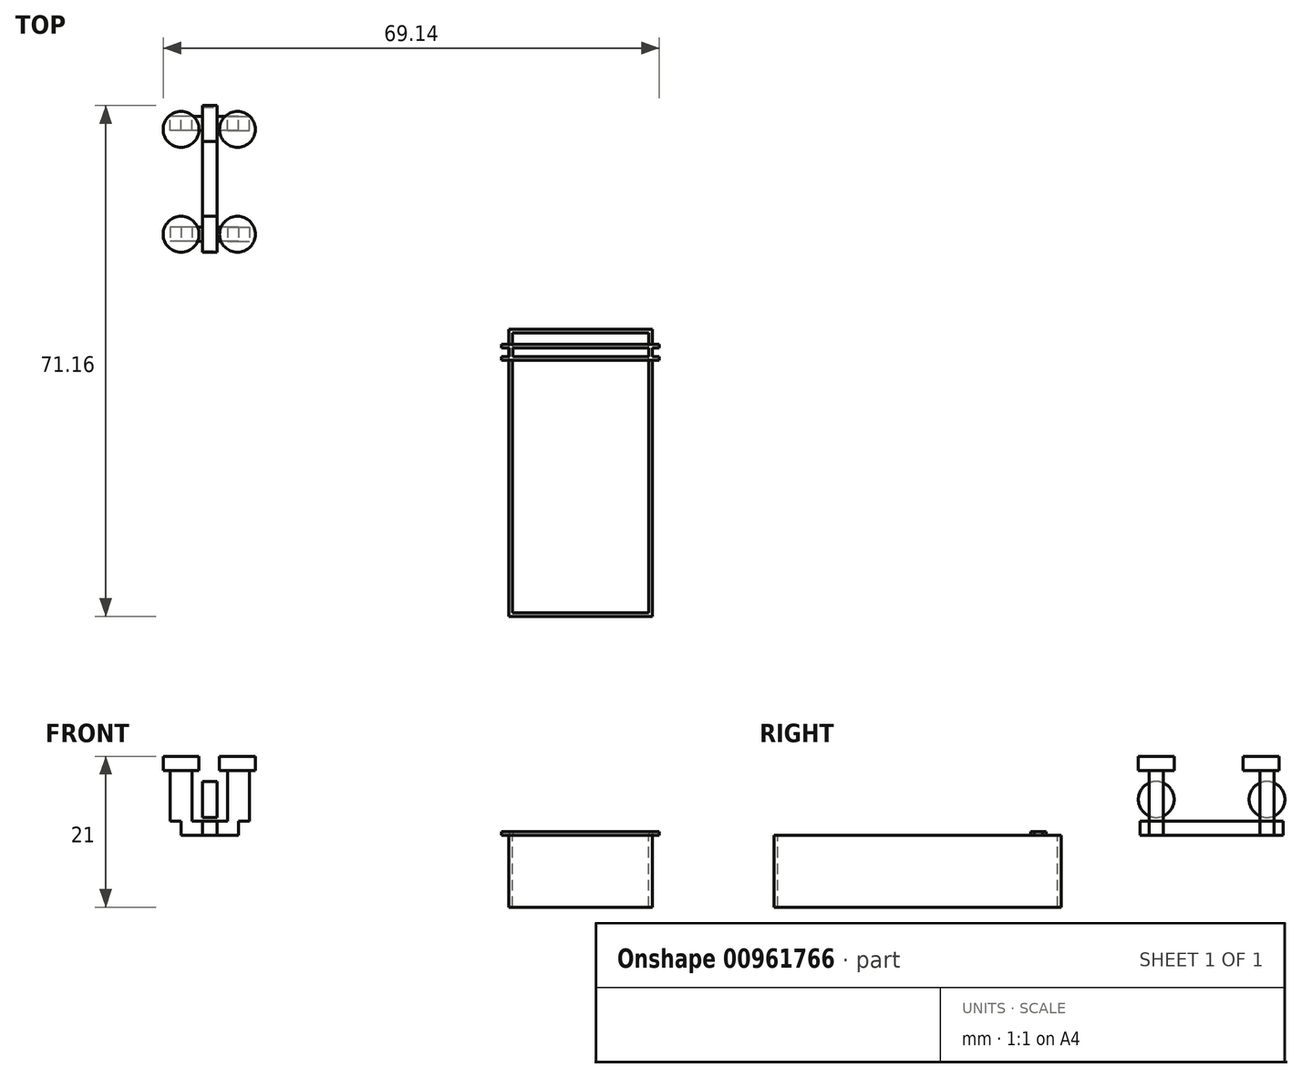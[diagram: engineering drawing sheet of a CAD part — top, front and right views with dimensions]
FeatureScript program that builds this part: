
annotation { "Feature Type Name" : "Feature", "Feature Type Description" : "" }
export const myFeature = defineFeature(function(context is Context, id is Id, definition is map)
    precondition{}
    {
        {
            var Q0;
            Q0=qCreatedBy(makeId("Top.planeOp"),FACE);
            var sketch = newSketch(context, id + "F0", { "sketchPlane" : qUnion([Q0])});
            skLineSegment(sketch, "E0.bottom", {"start": v(-9.2, 17.34) * mm, "end": v(10.8, 17.34) * mm});
            skLineSegment(sketch, "E0.top", {"start": v(-9.2, -22.66) * mm, "end": v(10.8, -22.66) * mm});
            skLineSegment(sketch, "E0.left", {"start": v(-9.2, 17.34) * mm, "end": v(-9.2, -22.66) * mm});
            skLineSegment(sketch, "E0.right", {"start": v(10.8, 17.34) * mm, "end": v(10.8, -22.66) * mm});
            skLineSegment(sketch, "E1.0", {"start": v(-8.7, 16.84) * mm, "end": v(10.3, 16.84) * mm});
            skLineSegment(sketch, "E1.1", {"start": v(-8.7, 16.84) * mm, "end": v(-8.7, -22.16) * mm});
            skLineSegment(sketch, "E1.2", {"start": v(-8.7, -22.16) * mm, "end": v(10.3, -22.16) * mm});
            skLineSegment(sketch, "E1.3", {"start": v(10.3, 16.84) * mm, "end": v(10.3, -22.16) * mm});
            skSolve(sketch);
        }
        {
            var Q0;
            Q0 = qSketchRegion(id + "F0", true);
            extrude(context, id + "F1", {"entities" : qUnion([Q0]), "depth" : -10 * mm, "offsetDistance" : 25 * mm});
        }
        {
            var Q0;
            Q0=qCreatedBy(makeId("Top.planeOp"),FACE);
            var sketch = newSketch(context, id + "F2", { "sketchPlane" : qUnion([Q0])});
            skLineSegment(sketch, "E2.bottom", {"start": v(-10.2, 15.22) * mm, "end": v(11.8, 15.22) * mm});
            skLineSegment(sketch, "E2.top", {"start": v(-10.2, 14.72) * mm, "end": v(11.8, 14.72) * mm});
            skLineSegment(sketch, "E2.left", {"start": v(-10.2, 15.22) * mm, "end": v(-10.2, 14.72) * mm});
            skLineSegment(sketch, "E2.right", {"start": v(11.8, 15.22) * mm, "end": v(11.8, 14.72) * mm});
            skLineSegment(sketch, "E3.bottom", {"start": v(-10.2, 13.55) * mm, "end": v(11.8, 13.55) * mm});
            skLineSegment(sketch, "E3.top", {"start": v(-10.2, 13.05) * mm, "end": v(11.8, 13.05) * mm});
            skLineSegment(sketch, "E3.left", {"start": v(-10.2, 13.55) * mm, "end": v(-10.2, 13.05) * mm});
            skLineSegment(sketch, "E3.right", {"start": v(11.8, 13.55) * mm, "end": v(11.8, 13.05) * mm});
            skLineSegment(sketch, "E4.bottom", {"start": v(-9.15, 15.22) * mm, "end": v(-8.62, 15.22) * mm});
            skLineSegment(sketch, "E4.top", {"start": v(-9.15, 13.05) * mm, "end": v(-8.62, 13.05) * mm});
            skLineSegment(sketch, "E4.left", {"start": v(-9.15, 15.22) * mm, "end": v(-9.15, 13.05) * mm});
            skLineSegment(sketch, "E4.right", {"start": v(-8.62, 15.22) * mm, "end": v(-8.62, 13.05) * mm});
            skLineSegment(sketch, "E5.bottom", {"start": v(10.81, 15.22) * mm, "end": v(10.29, 15.22) * mm});
            skLineSegment(sketch, "E5.top", {"start": v(10.81, 13.05) * mm, "end": v(10.29, 13.05) * mm});
            skLineSegment(sketch, "E5.left", {"start": v(10.81, 15.22) * mm, "end": v(10.81, 13.05) * mm});
            skLineSegment(sketch, "E5.right", {"start": v(10.29, 15.22) * mm, "end": v(10.29, 13.05) * mm});
            skSolve(sketch);
        }
        {
            var Q0;
            Q0 = qSketchRegion(id + "F2", true);
            extrude(context, id + "F3", {"entities" : qUnion([Q0]), "operationType" : NewBodyOperationType.ADD, "depth" : 0.5 * mm, "offsetDistance" : 25 * mm});
        }
        {
            var Q0;
            Q0=qCreatedBy(makeId("Top.planeOp"),FACE);
            var sketch = newSketch(context, id + "F4", { "sketchPlane" : qUnion([Q0])});
            skLineSegment(sketch, "E6.bottom", {"start": v(-51.85, 48.28) * mm, "end": v(-49.85, 48.28) * mm});
            skLineSegment(sketch, "E6.top", {"start": v(-51.85, 28.28) * mm, "end": v(-49.85, 28.28) * mm});
            skLineSegment(sketch, "E6.left", {"start": v(-51.85, 48.28) * mm, "end": v(-51.85, 28.28) * mm});
            skLineSegment(sketch, "E6.right", {"start": v(-49.85, 48.28) * mm, "end": v(-49.85, 28.28) * mm});
            skLineSegment(sketch, "E7.bottom", {"start": v(-46.85, 45) * mm, "end": v(-54.85, 45) * mm});
            skLineSegment(sketch, "E7.top", {"start": v(-46.85, 47) * mm, "end": v(-54.85, 47) * mm});
            skLineSegment(sketch, "E7.left", {"start": v(-46.85, 45) * mm, "end": v(-46.85, 47) * mm});
            skLineSegment(sketch, "E7.right", {"start": v(-54.85, 45) * mm, "end": v(-54.85, 47) * mm});
            skLineSegment(sketch, "E8.MirrorCS", {"start": v(-46.85, 31.56) * mm, "end": v(-54.85, 31.56) * mm});
            skLineSegment(sketch, "E9.MirrorCS", {"start": v(-54.85, 31.56) * mm, "end": v(-54.85, 29.56) * mm});
            skLineSegment(sketch, "E10.MirrorCS", {"start": v(-46.85, 29.56) * mm, "end": v(-54.85, 29.56) * mm});
            skLineSegment(sketch, "E11.MirrorCS", {"start": v(-46.85, 31.56) * mm, "end": v(-46.85, 29.56) * mm});
            skCircle(sketch, "E12", {"center": v(-46.86, 46.1) * mm, "radius": 2.5 * mm});
            skCircle(sketch, "E13", {"center": v(-54.85, 46) * mm, "radius": 2.5 * mm});
            skCircle(sketch, "E14.MirrorC", {"center": v(-46.86, 30.46) * mm, "radius": 2.5 * mm});
            skCircle(sketch, "E15.MirrorC", {"center": v(-54.85, 30.56) * mm, "radius": 2.5 * mm});
            skCircle(sketch, "E16", {"center": v(-54.85, 46) * mm, "radius": 0.7 * mm});
            skCircle(sketch, "E17.MirrorC", {"center": v(-54.85, 30.56) * mm, "radius": 0.7 * mm});
            skCircle(sketch, "E18.MirrorC", {"center": v(-46.85, 46) * mm, "radius": 0.7 * mm});
            skCircle(sketch, "E19.MirrorC", {"center": v(-46.85, 30.56) * mm, "radius": 0.7 * mm});
            skSolve(sketch);
        }
        {
            var Q0;
            {var subQ0=sQuery(id+"F4.wireOp",EDGE,"E6.bottom");Q0=makeQuery(id+"F4.imprint","IMPRINT",FACE,{"disambiguationData":[TD([[makeQuery(id+"F4.imprint","IMPRINT",EDGE,{"derivedFrom":subQ0}),-1.0]])]});}
            var Q1;
            {var subQ0=sQuery(id+"F4.wireOp",EDGE,"E6.top");Q1=makeQuery(id+"F4.imprint","IMPRINT",FACE,{"disambiguationData":[TD([[makeQuery(id+"F4.imprint","IMPRINT",EDGE,{"derivedFrom":subQ0}),1.0]])]});}
            var Q2;
            {var subQ0=sQuery(id+"F4.wireOp",EDGE,"E7.top");var subQ1=sQuery(id+"F4.wireOp",EDGE,"E6.left");var subQ2=makeQuery(id+"F4.imprint","INTERSECT",VERTEX,{"derivedFrom":[subQ1,subQ0]});Q2=makeQuery(id+"F4.imprint","IMPRINT",FACE,{"disambiguationData":[TD([[makeQuery(id+"F4.imprint","IMPRINT",EDGE,{"disambiguationData":[TD([[subQ2,-1.0]])],"derivedFrom":subQ1}),-1.0]])]});}
            var Q3;
            {var subQ0=sQuery(id+"F4.wireOp",EDGE,"E7.bottom");var subQ1=sQuery(id+"F4.wireOp",EDGE,"E6.left");var subQ2=makeQuery(id+"F4.imprint","INTERSECT",VERTEX,{"derivedFrom":[subQ1,subQ0]});Q3=makeQuery(id+"F4.imprint","IMPRINT",FACE,{"disambiguationData":[TD([[makeQuery(id+"F4.imprint","IMPRINT",EDGE,{"disambiguationData":[TD([[subQ2,-1.0]])],"derivedFrom":subQ1}),1.0]])]});}
            var Q4;
            {var subQ0=sQuery(id+"F4.wireOp",EDGE,"E8.MirrorCS");var subQ1=sQuery(id+"F4.wireOp",EDGE,"E6.left");var subQ2=makeQuery(id+"F4.imprint","INTERSECT",VERTEX,{"derivedFrom":[subQ1,subQ0]});Q4=makeQuery(id+"F4.imprint","IMPRINT",FACE,{"disambiguationData":[TD([[makeQuery(id+"F4.imprint","IMPRINT",EDGE,{"disambiguationData":[TD([[subQ2,-1.0]])],"derivedFrom":subQ1}),-1.0]])]});}
            var Q5;
            {var subQ0=sQuery(id+"F4.wireOp",EDGE,"E7.top");var subQ1=sQuery(id+"F4.wireOp",EDGE,"E6.right");var subQ2=makeQuery(id+"F4.imprint","INTERSECT",VERTEX,{"derivedFrom":[subQ1,subQ0]});Q5=makeQuery(id+"F4.imprint","IMPRINT",FACE,{"disambiguationData":[TD([[makeQuery(id+"F4.imprint","IMPRINT",EDGE,{"disambiguationData":[TD([[subQ2,-1.0]])],"derivedFrom":subQ1}),1.0]])]});}
            var Q6;
            {var subQ0=sQuery(id+"F4.wireOp",EDGE,"E8.MirrorCS");var subQ1=sQuery(id+"F4.wireOp",EDGE,"E6.right");var subQ2=makeQuery(id+"F4.imprint","INTERSECT",VERTEX,{"derivedFrom":[subQ1,subQ0]});Q6=makeQuery(id+"F4.imprint","IMPRINT",FACE,{"disambiguationData":[TD([[makeQuery(id+"F4.imprint","IMPRINT",EDGE,{"disambiguationData":[TD([[subQ2,-1.0]])],"derivedFrom":subQ1}),1.0]])]});}
            var Q7;
            {var subQ0=sQuery(id+"F4.wireOp",EDGE,"E7.left");var subQ6=sQuery(id+"F4.wireOp",EDGE,"E7.bottom");var subQ7=makeQuery(id+"F4.imprint","INTERSECT",VERTEX,{"derivedFrom":[subQ6,subQ0]});Q7=makeQuery(id+"F4.imprint","IMPRINT",FACE,{"disambiguationData":[TD([[makeQuery(id+"F4.imprint","IMPRINT",EDGE,{"disambiguationData":[TD([[subQ7,-1.0]])],"derivedFrom":subQ6}),-1.0]])]});}
            var Q8;
            {var subQ0=sQuery(id+"F4.wireOp",EDGE,"E11.MirrorCS");var subQ1=sQuery(id+"F4.wireOp",EDGE,"E8.MirrorCS");var subQ2=makeQuery(id+"F4.imprint","INTERSECT",VERTEX,{"derivedFrom":[subQ1,subQ0]});Q8=makeQuery(id+"F4.imprint","IMPRINT",FACE,{"disambiguationData":[TD([[makeQuery(id+"F4.imprint","IMPRINT",EDGE,{"disambiguationData":[TD([[subQ2,-1.0]])],"derivedFrom":subQ1}),1.0]])]});}
            var Q9;
            {var subQ1=sQuery(id+"F4.wireOp",EDGE,"E9.MirrorCS");var subQ5=sQuery(id+"F4.wireOp",EDGE,"E8.MirrorCS");var subQ9=makeQuery(id+"F4.imprint","INTERSECT",VERTEX,{"derivedFrom":[subQ5,subQ1]});Q9=makeQuery(id+"F4.imprint","IMPRINT",FACE,{"disambiguationData":[TD([[makeQuery(id+"F4.imprint","IMPRINT",EDGE,{"disambiguationData":[TD([[subQ9,1.0]])],"derivedFrom":subQ5}),1.0]])]});}
            var Q10;
            {var subQ0=sQuery(id+"F4.wireOp",EDGE,"E7.top");var subQ1=sQuery(id+"F4.wireOp",EDGE,"E6.left");var subQ2=makeQuery(id+"F4.imprint","INTERSECT",VERTEX,{"derivedFrom":[subQ1,subQ0]});Q10=makeQuery(id+"F4.imprint","IMPRINT",FACE,{"disambiguationData":[TD([[makeQuery(id+"F4.imprint","IMPRINT",EDGE,{"disambiguationData":[TD([[subQ2,-1.0]])],"derivedFrom":subQ1}),1.0]])]});}
            var Q11;
            {var subQ0=sQuery(id+"F4.wireOp",EDGE,"E8.MirrorCS");var subQ1=sQuery(id+"F4.wireOp",EDGE,"E6.left");var subQ2=makeQuery(id+"F4.imprint","INTERSECT",VERTEX,{"derivedFrom":[subQ1,subQ0]});Q11=makeQuery(id+"F4.imprint","IMPRINT",FACE,{"disambiguationData":[TD([[makeQuery(id+"F4.imprint","IMPRINT",EDGE,{"disambiguationData":[TD([[subQ2,-1.0]])],"derivedFrom":subQ1}),1.0]])]});}
            var Q12;
            {var subQ0=sQuery(id+"F4.wireOp",EDGE,"E7.right");var subQ5=sQuery(id+"F4.wireOp",EDGE,"E7.bottom");var subQ6=makeQuery(id+"F4.imprint","INTERSECT",VERTEX,{"derivedFrom":[subQ5,subQ0]});Q12=makeQuery(id+"F4.imprint","IMPRINT",FACE,{"disambiguationData":[TD([[makeQuery(id+"F4.imprint","IMPRINT",EDGE,{"disambiguationData":[TD([[subQ6,1.0]])],"derivedFrom":subQ5}),-1.0]])]});}
            var Q13;
            {var subQ0=sQuery(id+"F4.wireOp",EDGE,"E16");var subQ1=sQuery(id+"F4.wireOp",EDGE,"E7.right");var subQ2=makeQuery(id+"F4.imprint","INTERSECT",VERTEX,{"disambiguationData":[OD(0.0)],"derivedFrom":[subQ1,subQ0]});Q13=makeQuery(id+"F4.imprint","IMPRINT",FACE,{"disambiguationData":[TD([[makeQuery(id+"F4.imprint","IMPRINT",EDGE,{"disambiguationData":[TD([[subQ2,-1.0]])],"derivedFrom":subQ1}),-1.0]])]});}
            var Q14;
            {var subQ0=sQuery(id+"F4.wireOp",EDGE,"E18.MirrorC");var subQ1=sQuery(id+"F4.wireOp",EDGE,"E7.left");var subQ2=makeQuery(id+"F4.imprint","INTERSECT",VERTEX,{"disambiguationData":[OD(0.0)],"derivedFrom":[subQ1,subQ0]});Q14=makeQuery(id+"F4.imprint","IMPRINT",FACE,{"disambiguationData":[TD([[makeQuery(id+"F4.imprint","IMPRINT",EDGE,{"disambiguationData":[TD([[subQ2,-1.0]])],"derivedFrom":subQ1}),1.0]])]});}
            var Q15;
            {var subQ0=sQuery(id+"F4.wireOp",EDGE,"E19.MirrorC");var subQ1=sQuery(id+"F4.wireOp",EDGE,"E11.MirrorCS");var subQ2=makeQuery(id+"F4.imprint","INTERSECT",VERTEX,{"disambiguationData":[OD(0.0)],"derivedFrom":[subQ1,subQ0]});Q15=makeQuery(id+"F4.imprint","IMPRINT",FACE,{"disambiguationData":[TD([[makeQuery(id+"F4.imprint","IMPRINT",EDGE,{"disambiguationData":[TD([[subQ2,-1.0]])],"derivedFrom":subQ1}),-1.0]])]});}
            var Q16;
            {var subQ0=sQuery(id+"F4.wireOp",EDGE,"E17.MirrorC");var subQ1=sQuery(id+"F4.wireOp",EDGE,"E9.MirrorCS");var subQ2=makeQuery(id+"F4.imprint","INTERSECT",VERTEX,{"disambiguationData":[OD(0.0)],"derivedFrom":[subQ1,subQ0]});Q16=makeQuery(id+"F4.imprint","IMPRINT",FACE,{"disambiguationData":[TD([[makeQuery(id+"F4.imprint","IMPRINT",EDGE,{"disambiguationData":[TD([[subQ2,-1.0]])],"derivedFrom":subQ1}),1.0]])]});}
            extrude(context, id + "F5", {"entities" : qUnion([Q0, Q1, Q2, Q3, Q4, Q5, Q6, Q7, Q8, Q9, Q10, Q11, Q12, Q13, Q14, Q15, Q16]), "depth" : 2 * mm, "offsetDistance" : 25 * mm});
        }
        {
            var Q0;
            Q0=makeQuery(id+"F5.opExtrude","CAP_FACE",FACE,{"disambiguationData":[OSD([sQuery(id+"F4.wireOp",EDGE,"E6.bottom"),sQuery(id+"F4.wireOp",EDGE,"E6.top"),sQuery(id+"F4.wireOp",EDGE,"E6.left"),sQuery(id+"F4.wireOp",EDGE,"E6.right"),sQuery(id+"F4.wireOp",EDGE,"E7.bottom"),sQuery(id+"F4.wireOp",EDGE,"E7.top"),sQuery(id+"F4.wireOp",EDGE,"E7.left"),sQuery(id+"F4.wireOp",EDGE,"E7.right"),sQuery(id+"F4.wireOp",EDGE,"E8.MirrorCS"),sQuery(id+"F4.wireOp",EDGE,"E9.MirrorCS"),sQuery(id+"F4.wireOp",EDGE,"E10.MirrorCS"),sQuery(id+"F4.wireOp",EDGE,"E11.MirrorCS")])],"isStart":false});
            var sketch = newSketch(context, id + "F6", { "sketchPlane" : qUnion([Q0])});
            skLineSegment(sketch, "E20.bottom", {"start": v(-53.35, 45) * mm, "end": v(-56.35, 45) * mm});
            skLineSegment(sketch, "E20.top", {"start": v(-53.35, 47) * mm, "end": v(-56.35, 47) * mm});
            skLineSegment(sketch, "E20.left", {"start": v(-53.35, 45) * mm, "end": v(-53.35, 47) * mm});
            skLineSegment(sketch, "E20.right", {"start": v(-56.35, 45) * mm, "end": v(-56.35, 47) * mm});
            skLineSegment(sketch, "E21", {"start": v(-50.85, 48.28) * mm, "end": v(-50.85, 28.28) * mm});
            skLineSegment(sketch, "E22", {"start": v(-51.85, 38.28) * mm, "end": v(-49.85, 38.28) * mm});
            skLineSegment(sketch, "E23.MirrorCS", {"start": v(-45.35, 45) * mm, "end": v(-45.35, 47) * mm});
            skLineSegment(sketch, "E24.MirrorCS", {"start": v(-48.35, 47) * mm, "end": v(-45.35, 47) * mm});
            skLineSegment(sketch, "E25.MirrorCS", {"start": v(-48.35, 45) * mm, "end": v(-48.35, 47) * mm});
            skLineSegment(sketch, "E26.MirrorCS", {"start": v(-48.35, 45) * mm, "end": v(-45.35, 45) * mm});
            skLineSegment(sketch, "E27.MirrorCS", {"start": v(-48.35, 31.56) * mm, "end": v(-48.35, 29.56) * mm});
            skLineSegment(sketch, "E28.MirrorCS", {"start": v(-48.35, 31.56) * mm, "end": v(-45.35, 31.56) * mm});
            skLineSegment(sketch, "E29.MirrorCS", {"start": v(-48.35, 29.56) * mm, "end": v(-45.35, 29.56) * mm});
            skLineSegment(sketch, "E30.MirrorCS", {"start": v(-45.35, 31.56) * mm, "end": v(-45.35, 29.56) * mm});
            skLineSegment(sketch, "E31.MirrorCS", {"start": v(-53.35, 31.56) * mm, "end": v(-56.35, 31.56) * mm});
            skLineSegment(sketch, "E32.MirrorCS", {"start": v(-56.35, 31.56) * mm, "end": v(-56.35, 29.56) * mm});
            skLineSegment(sketch, "E33.MirrorCS", {"start": v(-53.35, 29.56) * mm, "end": v(-56.35, 29.56) * mm});
            skLineSegment(sketch, "E34.MirrorCS", {"start": v(-53.35, 31.56) * mm, "end": v(-53.35, 29.56) * mm});
            skSolve(sketch);
        }
        {
            var Q0;
            Q0 = qSketchRegion(id + "F6", true);
            extrude(context, id + "F7", {"entities" : qUnion([Q0]), "operationType" : NewBodyOperationType.ADD, "depth" : 7 * mm, "offsetDistance" : 25 * mm});
        }
        {
            var Q0;
            Q0=makeQuery(id+"F7.opExtrude","CAP_FACE",FACE,{"disambiguationData":[OSD([sQuery(id+"F6.wireOp",EDGE,"E31.MirrorCS"),sQuery(id+"F6.wireOp",EDGE,"E32.MirrorCS"),sQuery(id+"F6.wireOp",EDGE,"E33.MirrorCS"),sQuery(id+"F6.wireOp",EDGE,"E34.MirrorCS")])],"isStart":false});
            var sketch = newSketch(context, id + "F8", { "sketchPlane" : qUnion([Q0])});
            skCircle(sketch, "E35", {"center": v(-54.85, 30.56) * mm, "radius": 2.5 * mm});
            skCircle(sketch, "E36.MirrorC", {"center": v(-46.99, 30.56) * mm, "radius": 2.5 * mm});
            skCircle(sketch, "E37.MirrorC", {"center": v(-46.99, 45.18) * mm, "radius": 2.5 * mm});
            skCircle(sketch, "E38.MirrorC", {"center": v(-54.85, 45.18) * mm, "radius": 2.5 * mm});
            skSolve(sketch);
        }
        {
            var Q0;
            Q0 = qSketchRegion(id + "F8", true);
            extrude(context, id + "F9", {"entities" : qUnion([Q0]), "operationType" : NewBodyOperationType.ADD, "depth" : 2 * mm, "offsetDistance" : 25 * mm});
        }
        {
            var Q0;
            {var subQ0=sQuery(id+"F4.wireOp",EDGE,"E6.left");Q0=makeQuery(id+"F5.opExtrude","SWEPT_FACE",FACE,{"disambiguationData":[OSD([subQ0]),TDD([makeQuery(id+"F4.imprint","IMPRINT",EDGE,{"disambiguationData":[TD([[makeQuery(id+"F4.imprint","INTERSECT",VERTEX,{"derivedFrom":[subQ0,sQuery(id+"F4.wireOp",EDGE,"E7.bottom")]}),-1.0]])],"derivedFrom":subQ0})])]});}
            var sketch = newSketch(context, id + "F10", { "sketchPlane" : qUnion([Q0])});
            skLineSegment(sketch, "E39.left", {"start": v(-45, 0) * mm, "end": v(-45, 5) * mm});
            skLineSegment(sketch, "E40.left", {"start": v(-45, 5) * mm, "end": v(-45, 4.26) * mm});
            skCircle(sketch, "E41", {"center": v(-46, 5) * mm, "radius": 2.5 * mm});
            skCircle(sketch, "E42.MirrorC", {"center": v(-30.56, 5) * mm, "radius": 2.5 * mm});
            skSolve(sketch);
        }
        {
            var Q0;
            Q0 = qSketchRegion(id + "F10", true);
            extrude(context, id + "F11", {"entities" : qUnion([Q0]), "depth" : -2 * mm, "offsetDistance" : 25 * mm});
        }
    });
